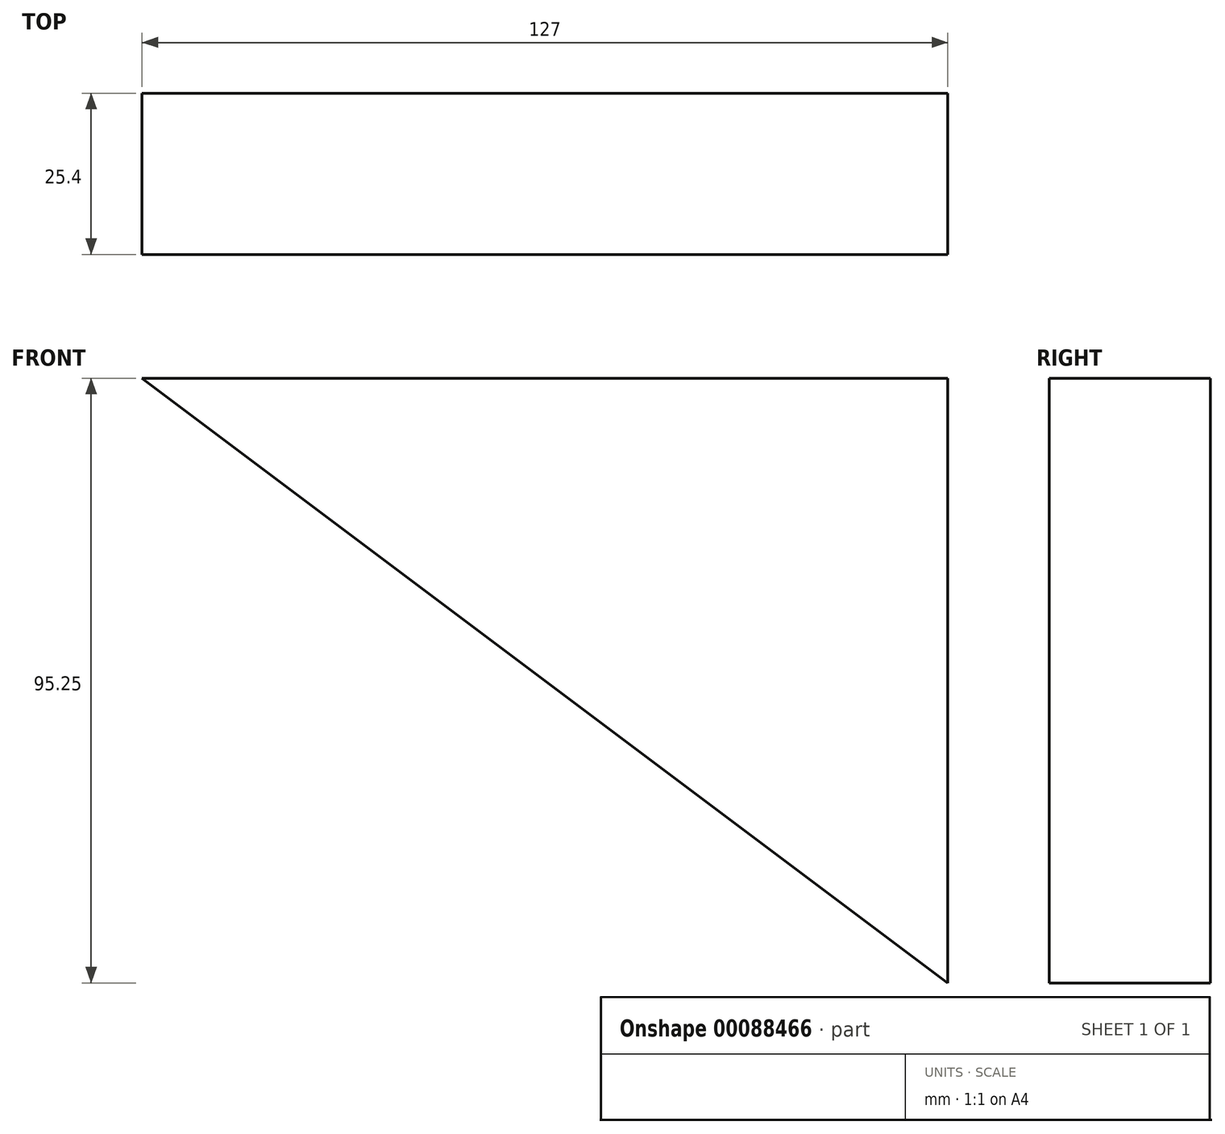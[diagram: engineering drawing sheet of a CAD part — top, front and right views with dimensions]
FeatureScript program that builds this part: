
annotation { "Feature Type Name" : "Feature", "Feature Type Description" : "" }
export const myFeature = defineFeature(function(context is Context, id is Id, definition is map)
    precondition{}
    {
        {
            var Q0;
            Q0=qCreatedBy(makeId("Front.planeOp"),FACE);
            var sketch = newSketch(context, id + "F0", { "sketchPlane" : qUnion([Q0])});
            skLineSegment(sketch, "E0", {"start": v(0, 0) * mm, "end": v(127, 0) * mm});
            skLineSegment(sketch, "E1", {"start": v(127, 0) * mm, "end": v(127, -95.25) * mm});
            skLineSegment(sketch, "E2", {"start": v(127, -95.25) * mm, "end": v(0, 0) * mm});
            skSolve(sketch);
        }
        {
            var Q0;
            Q0 = qSketchRegion(id + "F0", true);
            extrude(context, id + "F1", {"entities" : qUnion([Q0]), "depth" : 25.4 * mm});
        }
    });
